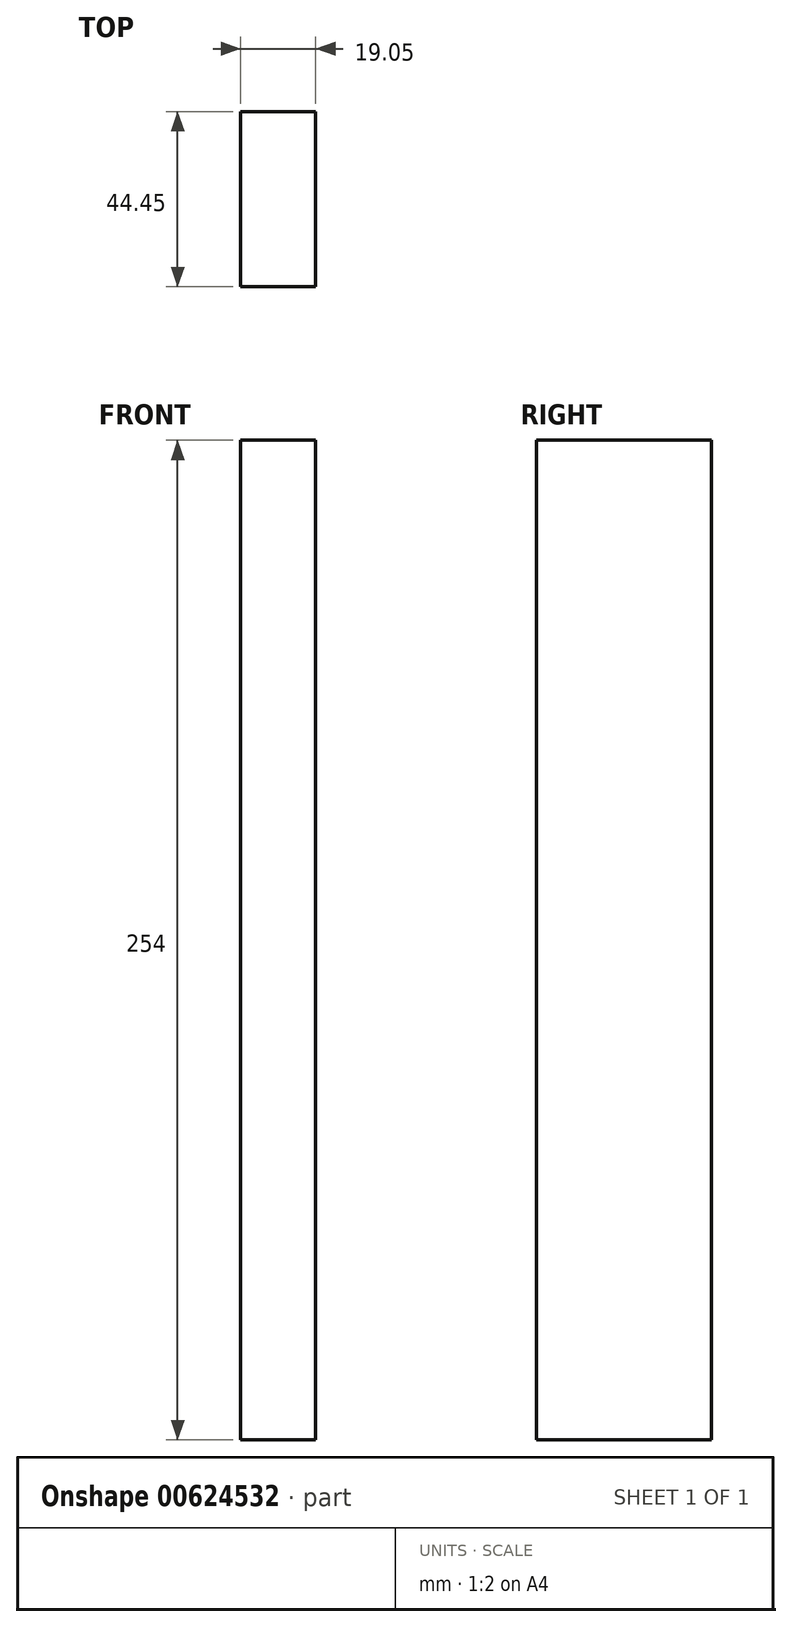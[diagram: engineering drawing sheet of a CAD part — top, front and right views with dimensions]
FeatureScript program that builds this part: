
annotation { "Feature Type Name" : "Feature", "Feature Type Description" : "" }
export const myFeature = defineFeature(function(context is Context, id is Id, definition is map)
    precondition{}
    {
        {
            var Q0;
            Q0=qCreatedBy(makeId("Right.planeOp"),FACE);
            var sketch = newSketch(context, id + "F0", { "sketchPlane" : qUnion([Q0])});
            skLineSegment(sketch, "E0.bottom", {"start": v(0, 0) * mm, "end": v(44.45, 0) * mm});
            skLineSegment(sketch, "E0.top", {"start": v(0, 254) * mm, "end": v(44.45, 254) * mm});
            skLineSegment(sketch, "E0.left", {"start": v(0, 0) * mm, "end": v(0, 254) * mm});
            skLineSegment(sketch, "E0.right", {"start": v(44.45, 0) * mm, "end": v(44.45, 254) * mm});
            skSolve(sketch);
        }
        {
            var Q0;
            Q0=makeQuery(id+"F0.imprint","IMPRINT",FACE,{"disambiguationData":[TD([[makeQuery(id+"F0.imprint","IMPRINT",EDGE,{"derivedFrom":sQuery(id+"F0.wireOp",EDGE,"E0.bottom")}),1.0]])]});
            extrude(context, id + "F1", {"entities" : qUnion([Q0]), "depth" : 19.05 * mm, "offsetDistance" : 25.4 * mm});
        }
    });
